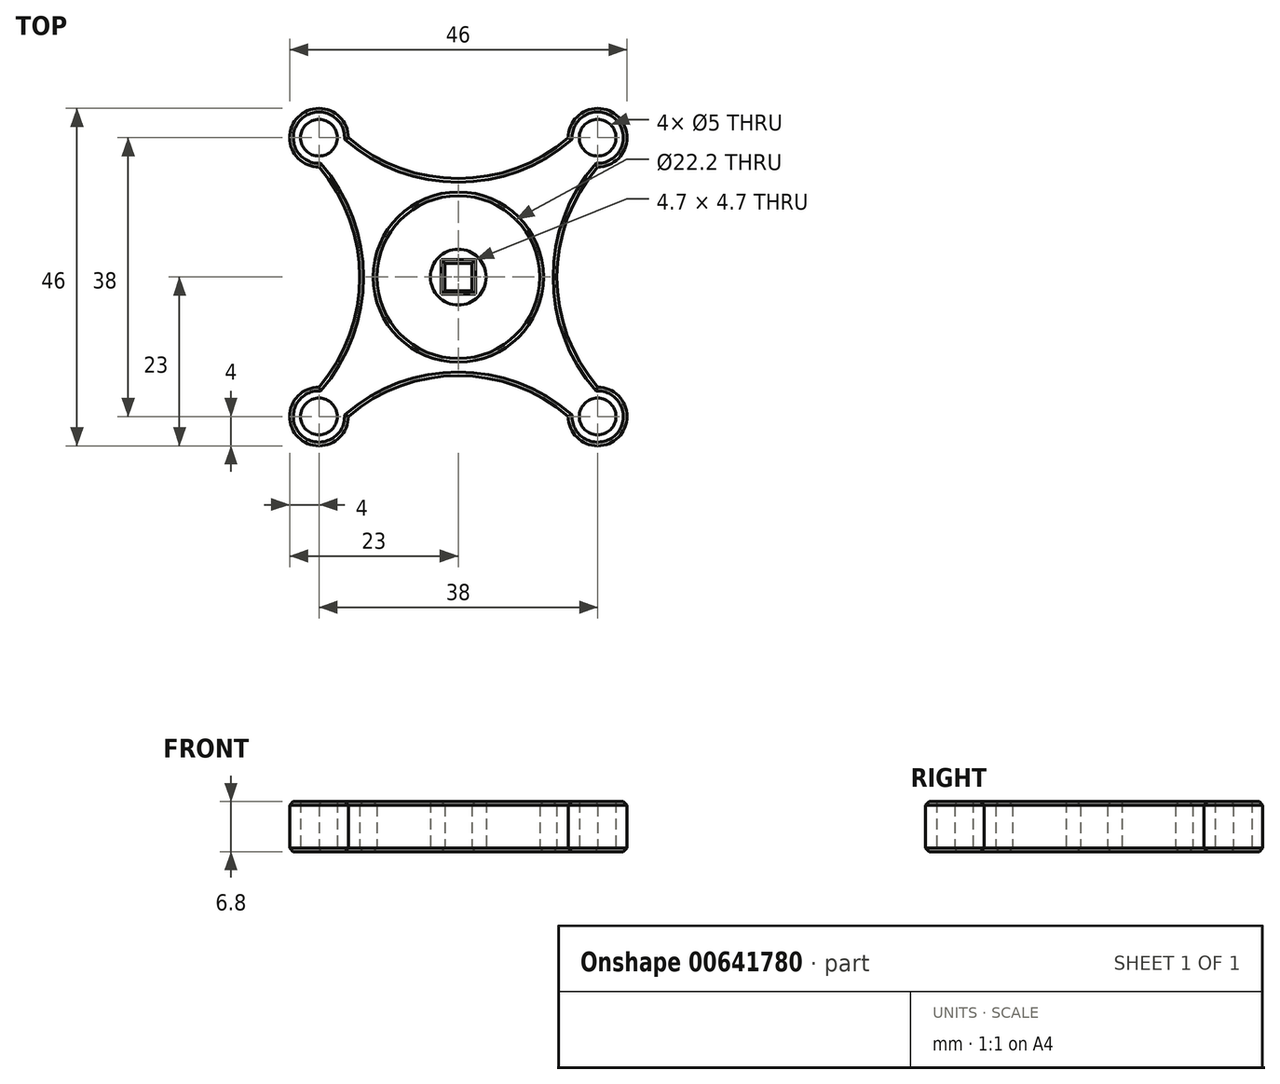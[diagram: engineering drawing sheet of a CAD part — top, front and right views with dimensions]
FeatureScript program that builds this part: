
annotation { "Feature Type Name" : "Feature", "Feature Type Description" : "" }
export const myFeature = defineFeature(function(context is Context, id is Id, definition is map)
    precondition{}
    {
        {
            var Q0;
            Q0=qCreatedBy(makeId("Top.planeOp"),FACE);
            var sketch = newSketch(context, id + "F0", { "sketchPlane" : qUnion([Q0])});
            skCircle(sketch, "E0", {"center": v(0, 0) * mm, "radius": 11.1 * mm});
            skCircle(sketch, "E1", {"center": v(-19, -19) * mm, "radius": 2.5 * mm});
            skCircle(sketch, "E2", {"center": v(-19, 19) * mm, "radius": 2.5 * mm});
            skCircle(sketch, "E3", {"center": v(19, 19) * mm, "radius": 2.5 * mm});
            skCircle(sketch, "E4", {"center": v(19, -19) * mm, "radius": 2.5 * mm});
            skArc(sketch, "E5", {"start": v(-19, -15) * mm, "mid": v(-21.83, -21.83) * mm, "end": v(-15, -19) * mm});
            skArc(sketch, "E6", {"start": v(15, -19) * mm, "mid": v(21.83, -21.83) * mm, "end": v(19, -15) * mm});
            skArc(sketch, "E7", {"start": v(19, 15) * mm, "mid": v(21.83, 21.83) * mm, "end": v(15, 19) * mm});
            skArc(sketch, "E8", {"start": v(-15, 19) * mm, "mid": v(-21.83, 21.83) * mm, "end": v(-19, 15) * mm});
            skArc(sketch, "E9", {"start": v(-19, -15) * mm, "mid": v(-13.44, 0) * mm, "end": v(-19, 15) * mm});
            skArc(sketch, "E10", {"start": v(15, -19) * mm, "mid": v(0, -13.44) * mm, "end": v(-15, -19) * mm});
            skArc(sketch, "E11", {"start": v(19, 15) * mm, "mid": v(13.44, 0) * mm, "end": v(19, -15) * mm});
            skArc(sketch, "E12", {"start": v(-15, 19) * mm, "mid": v(0, 13.44) * mm, "end": v(15, 19) * mm});
            skPoint(sketch, "E13.top.start.orphan", {"position": v(-12.5, 12.5) * mm});
            skPoint(sketch, "E13.bottom.start.orphan", {"position": v(-12.5, -12.5) * mm});
            skPoint(sketch, "E13.right.end.orphan", {"position": v(12.5, 12.5) * mm});
            skPoint(sketch, "E13.right.start.orphan", {"position": v(12.5, -12.5) * mm});
            skLineSegment(sketch, "E14", {"start": v(-19, 15) * mm, "end": v(-19, -15) * mm});
            skLineSegment(sketch, "E15", {"start": v(-15, 19) * mm, "end": v(15, 19) * mm});
            skLineSegment(sketch, "E16", {"start": v(19, 15) * mm, "end": v(19, -15) * mm});
            skLineSegment(sketch, "E17", {"start": v(15, -19) * mm, "end": v(-15, -19) * mm});
            skCircle(sketch, "E18", {"center": v(0, 0) * mm, "radius": 3.8 * mm});
            skLineSegment(sketch, "E19.bottom", {"start": v(1.85, -1.85) * mm, "end": v(-1.85, -1.85) * mm});
            skLineSegment(sketch, "E19.top", {"start": v(1.85, 1.85) * mm, "end": v(-1.85, 1.85) * mm});
            skLineSegment(sketch, "E19.left", {"start": v(1.85, -1.85) * mm, "end": v(1.85, 1.85) * mm});
            skLineSegment(sketch, "E19.right", {"start": v(-1.85, -1.85) * mm, "end": v(-1.85, 1.85) * mm});
            skSolve(sketch);
        }
        {
            var Q0;
            Q0=makeQuery(id+"F0.imprint","IMPRINT",FACE,{"disambiguationData":[TD([[makeQuery(id+"F0.imprint","IMPRINT",EDGE,{"derivedFrom":sQuery(id+"F0.wireOp",EDGE,"E0")}),-1.0]])]});
            var Q1;
            Q1=makeQuery(id+"F0.imprint","IMPRINT",FACE,{"disambiguationData":[TD([[makeQuery(id+"F0.imprint","IMPRINT",EDGE,{"derivedFrom":sQuery(id+"F0.wireOp",EDGE,"E18")}),1.0]])]});
            extrude(context, id + "F1", {"entities" : qUnion([Q0, Q1]), "depth" : 6.8 * mm, "offsetDistance" : 25 * mm});
        }
        {
            var Q0;
            Q0=makeQuery(id+"F1.opExtrude","CAP_EDGE",EDGE,{"disambiguationData":[OSD([sQuery(id+"F0.wireOp",EDGE,"E9")])],"isStart":false});
            var Q1;
            Q1=makeQuery(id+"F1.opExtrude","CAP_EDGE",EDGE,{"disambiguationData":[OSD([sQuery(id+"F0.wireOp",EDGE,"E8")])],"isStart":false});
            var Q2;
            Q2=makeQuery(id+"F1.opExtrude","CAP_EDGE",EDGE,{"disambiguationData":[OSD([sQuery(id+"F0.wireOp",EDGE,"E12")])],"isStart":false});
            var Q3;
            Q3=makeQuery(id+"F1.opExtrude","CAP_EDGE",EDGE,{"disambiguationData":[OSD([sQuery(id+"F0.wireOp",EDGE,"E7")])],"isStart":false});
            var Q4;
            Q4=makeQuery(id+"F1.opExtrude","CAP_EDGE",EDGE,{"disambiguationData":[OSD([sQuery(id+"F0.wireOp",EDGE,"E11")])],"isStart":false});
            var Q5;
            Q5=makeQuery(id+"F1.opExtrude","CAP_EDGE",EDGE,{"disambiguationData":[OSD([sQuery(id+"F0.wireOp",EDGE,"E6")])],"isStart":false});
            var Q6;
            Q6=makeQuery(id+"F1.opExtrude","CAP_EDGE",EDGE,{"disambiguationData":[OSD([sQuery(id+"F0.wireOp",EDGE,"E10")])],"isStart":false});
            var Q7;
            Q7=makeQuery(id+"F1.opExtrude","CAP_EDGE",EDGE,{"disambiguationData":[OSD([sQuery(id+"F0.wireOp",EDGE,"E5")])],"isStart":false});
            var Q8;
            Q8=makeQuery(id+"F1.opExtrude","CAP_EDGE",EDGE,{"disambiguationData":[OSD([sQuery(id+"F0.wireOp",EDGE,"E5")])],"isStart":true});
            var Q9;
            Q9=makeQuery(id+"F1.opExtrude","CAP_EDGE",EDGE,{"disambiguationData":[OSD([sQuery(id+"F0.wireOp",EDGE,"E9")])],"isStart":true});
            var Q10;
            Q10=makeQuery(id+"F1.opExtrude","CAP_EDGE",EDGE,{"disambiguationData":[OSD([sQuery(id+"F0.wireOp",EDGE,"E8")])],"isStart":true});
            var Q11;
            Q11=makeQuery(id+"F1.opExtrude","CAP_EDGE",EDGE,{"disambiguationData":[OSD([sQuery(id+"F0.wireOp",EDGE,"E10")])],"isStart":true});
            var Q12;
            Q12=makeQuery(id+"F1.opExtrude","CAP_EDGE",EDGE,{"disambiguationData":[OSD([sQuery(id+"F0.wireOp",EDGE,"E6")])],"isStart":true});
            var Q13;
            Q13=makeQuery(id+"F1.opExtrude","CAP_EDGE",EDGE,{"disambiguationData":[OSD([sQuery(id+"F0.wireOp",EDGE,"E11")])],"isStart":true});
            var Q14;
            Q14=makeQuery(id+"F1.opExtrude","CAP_EDGE",EDGE,{"disambiguationData":[OSD([sQuery(id+"F0.wireOp",EDGE,"E7")])],"isStart":true});
            var Q15;
            Q15=makeQuery(id+"F1.opExtrude","CAP_EDGE",EDGE,{"disambiguationData":[OSD([sQuery(id+"F0.wireOp",EDGE,"E12")])],"isStart":true});
            chamfer(context, id + "F2", {"entities" : qUnion([Q0, Q1, Q2, Q3, Q4, Q5, Q6, Q7, Q8, Q9, Q10, Q11, Q12, Q13, Q14, Q15]), "width" : .5 * mm, "tangentPropagation" : true});
        }
        {
            var Q0;
            Q0=makeQuery(id+"F1.opExtrude","CAP_EDGE",EDGE,{"disambiguationData":[OSD([sQuery(id+"F0.wireOp",EDGE,"E0")])],"isStart":false});
            var Q1;
            Q1=makeQuery(id+"F1.opExtrude","CAP_EDGE",EDGE,{"disambiguationData":[OSD([sQuery(id+"F0.wireOp",EDGE,"E0")])],"isStart":true});
            chamfer(context, id + "F3", {"entities" : qUnion([Q0, Q1]), "width" : .5 * mm, "tangentPropagation" : true});
        }
        {
            var Q0;
            Q0=makeQuery(id+"F1.opExtrude","CAP_EDGE",EDGE,{"disambiguationData":[OSD([sQuery(id+"F0.wireOp",EDGE,"E19.bottom")])],"isStart":false});
            var Q1;
            Q1=makeQuery(id+"F1.opExtrude","CAP_EDGE",EDGE,{"disambiguationData":[OSD([sQuery(id+"F0.wireOp",EDGE,"E19.right")])],"isStart":false});
            var Q2;
            Q2=makeQuery(id+"F1.opExtrude","CAP_EDGE",EDGE,{"disambiguationData":[OSD([sQuery(id+"F0.wireOp",EDGE,"E19.top")])],"isStart":false});
            var Q3;
            Q3=makeQuery(id+"F1.opExtrude","CAP_EDGE",EDGE,{"disambiguationData":[OSD([sQuery(id+"F0.wireOp",EDGE,"E19.left")])],"isStart":false});
            var Q4;
            Q4=makeQuery(id+"F1.opExtrude","CAP_EDGE",EDGE,{"disambiguationData":[OSD([sQuery(id+"F0.wireOp",EDGE,"E19.top")])],"isStart":true});
            var Q5;
            Q5=makeQuery(id+"F1.opExtrude","CAP_EDGE",EDGE,{"disambiguationData":[OSD([sQuery(id+"F0.wireOp",EDGE,"E19.right")])],"isStart":true});
            var Q6;
            Q6=makeQuery(id+"F1.opExtrude","CAP_EDGE",EDGE,{"disambiguationData":[OSD([sQuery(id+"F0.wireOp",EDGE,"E19.bottom")])],"isStart":true});
            var Q7;
            Q7=makeQuery(id+"F1.opExtrude","CAP_EDGE",EDGE,{"disambiguationData":[OSD([sQuery(id+"F0.wireOp",EDGE,"E19.left")])],"isStart":true});
            chamfer(context, id + "F4", {"entities" : qUnion([Q0, Q1, Q2, Q3, Q4, Q5, Q6, Q7]), "width" : .5 * mm, "tangentPropagation" : true});
        }
    });
